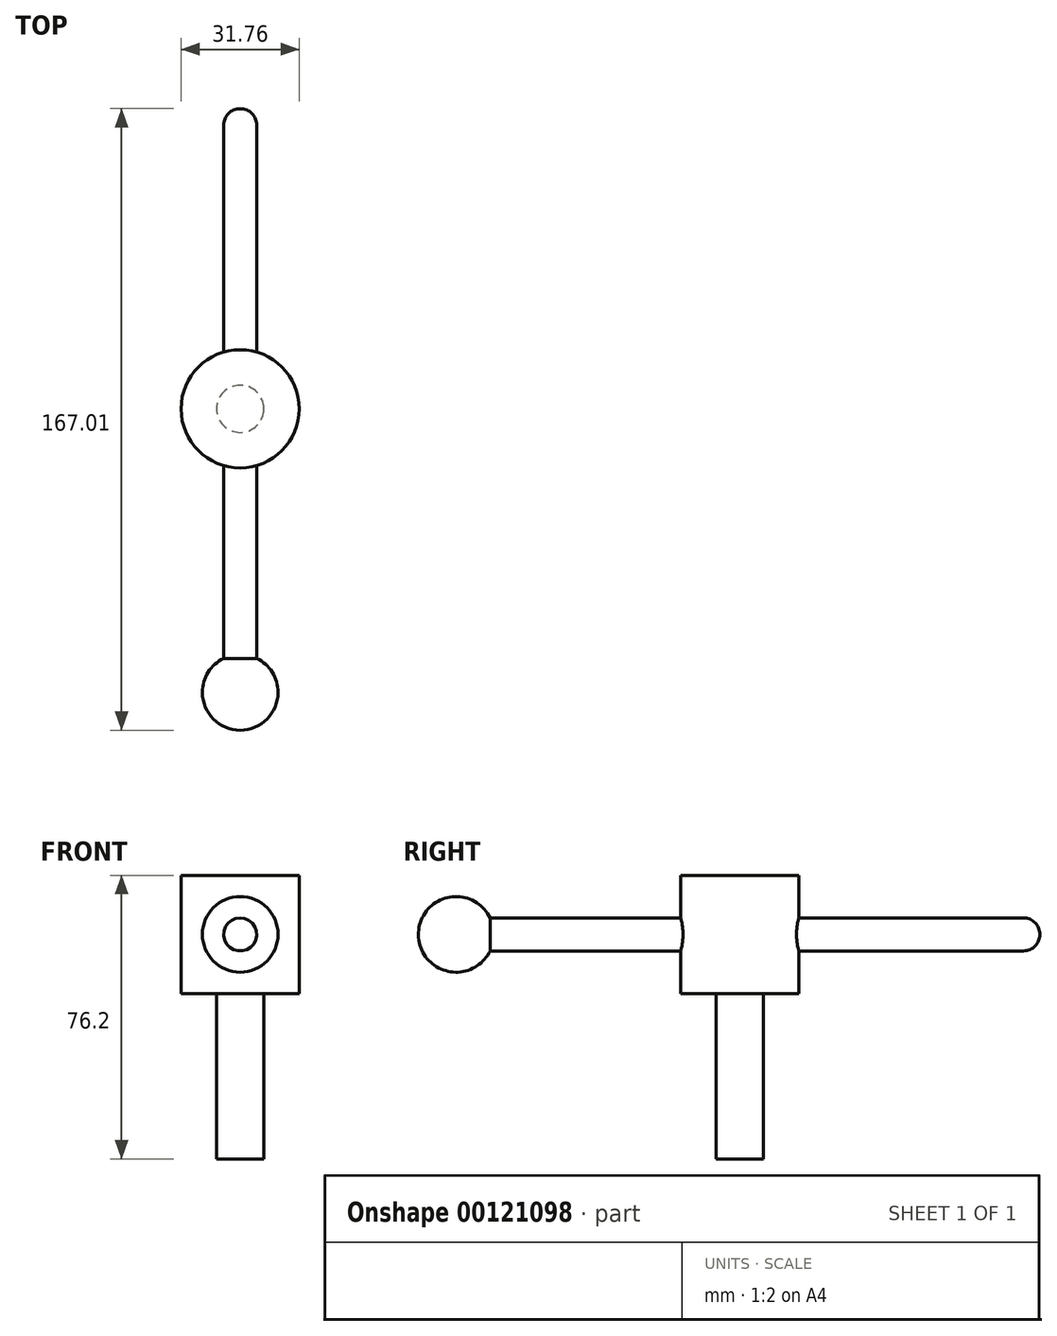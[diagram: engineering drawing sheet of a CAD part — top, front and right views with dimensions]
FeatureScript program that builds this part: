
annotation { "Feature Type Name" : "Feature", "Feature Type Description" : "" }
export const myFeature = defineFeature(function(context is Context, id is Id, definition is map)
    precondition{}
    {
        {
            var Q0;
            Q0=qCreatedBy(makeId("Right.planeOp"),FACE);
            var sketch = newSketch(context, id + "F0", { "sketchPlane" : qUnion([Q0])});
            skLineSegment(sketch, "E0.bottom", {"start": v(0, 0) * mm, "end": v(-6.35, 0) * mm});
            skLineSegment(sketch, "E0.top", {"start": v(0, 76.2) * mm, "end": v(-15.88, 76.2) * mm});
            skLineSegment(sketch, "E0.left", {"start": v(0, 0) * mm, "end": v(0, 76.2) * mm});
            skLineSegment(sketch, "E0.right", {"start": v(-15.88, 44.45) * mm, "end": v(-15.88, 76.2) * mm});
            skLineSegment(sketch, "E1", {"start": v(-15.88, 44.45) * mm, "end": v(-6.35, 44.45) * mm});
            skLineSegment(sketch, "E2", {"start": v(-6.35, 44.45) * mm, "end": v(-6.35, 0) * mm});
            skSolve(sketch);
        }
        {
            var Q0;
            Q0 = qSketchRegion(id + "F0", true);
            var Q1;
            Q1=sQuery(id+"F0.wireOp",EDGE,"E0.left");
            revolve(context, id + "F1", {"entities" : qUnion([Q0]), "axis" : qUnion([Q1]), "revolveType" : RevolveType.FULL});
        }
        {
            var Q0;
            Q0=qCreatedBy(makeId("Front.planeOp"),FACE);
            var sketch = newSketch(context, id + "F2", { "sketchPlane" : qUnion([Q0])});
            skCircle(sketch, "E3", {"center": v(0, 60.33) * mm, "radius": 4.45 * mm});
            skSolve(sketch);
        }
        {
            var Q0;
            Q0 = qSketchRegion(id + "F2", true);
            extrude(context, id + "F3", {"entities" : qUnion([Q0]), "operationType" : NewBodyOperationType.ADD, "endBound" : BoundingType.SYMMETRIC, "depth" : 152.4 * mm});
        }
        {
            var Q0;
            Q0=makeQuery(id+"F3.opExtrude","CAP_FACE",FACE,{"disambiguationData":[OSD([sQuery(id+"F2.wireOp",EDGE,"E3")])],"isStart":true});
            var sketch = newSketch(context, id + "F4", { "sketchPlane" : qUnion([Q0])});
            skArc(sketch, "E4", {"start": v(-10.16, 60.33) * mm, "mid": v(0, 70.48) * mm, "end": v(10.16, 60.33) * mm});
            skLineSegment(sketch, "E5", {"start": v(-10.16, 60.33) * mm, "end": v(10.16, 60.33) * mm});
            skSolve(sketch);
        }
        {
            var Q0;
            {var subQ0=sQuery(id+"F4.wireOp",EDGE,"E4");Q0=makeQuery(id+"F4.imprint","IMPRINT",FACE,{"disambiguationData":[TD([[makeQuery(id+"F4.imprint","IMPRINT",EDGE,{"derivedFrom":subQ0}),-1.0]])]});}
            var Q1;
            {var subQ0=sQuery(id+"F4.wireOp",EDGE,"E5");var subQ1=makeQuery(id+"F3.opExtrude","CAP_EDGE",EDGE,{"disambiguationData":[OSD([sQuery(id+"F2.wireOp",EDGE,"E3")])],"isStart":true});var subQ2=makeQuery(id+"F4.imprint","INTERSECT",VERTEX,{"disambiguationData":[OD(0.0)],"derivedFrom":[subQ1,subQ0]});Q1=makeQuery(id+"F4.imprint","IMPRINT",FACE,{"disambiguationData":[TD([[makeQuery(id+"F4.imprint","IMPRINT",EDGE,{"disambiguationData":[TD([[subQ2,-1.0]])],"derivedFrom":subQ0}),1.0]])]});}
            var Q2;
            Q2=sQuery(id+"F4.wireOp",EDGE,"E5");
            revolve(context, id + "F5", {"operationType" : NewBodyOperationType.ADD, "entities" : qUnion([Q0, Q1]), "axis" : qUnion([Q2]), "revolveType" : RevolveType.FULL});
        }
        {
            var Q0;
            Q0=makeQuery(id+"F3.opExtrude","CAP_FACE",FACE,{"disambiguationData":[OSD([sQuery(id+"F2.wireOp",EDGE,"E3")])],"isStart":false});
            var sketch = newSketch(context, id + "F6", { "sketchPlane" : qUnion([Q0])});
            skArc(sketch, "E6", {"start": v(-10.16, 60.33) * mm, "mid": v(0, 70.48) * mm, "end": v(10.16, 60.33) * mm});
            skLineSegment(sketch, "E7", {"start": v(-10.16, 60.33) * mm, "end": v(10.16, 60.33) * mm});
            skSolve(sketch);
        }
        {
            var Q0;
            Q0 = qSketchRegion(id + "F6", true);
            var Q1;
            Q1=sQuery(id+"F6.wireOp",EDGE,"E7");
            revolve(context, id + "F7", {"operationType" : NewBodyOperationType.ADD, "entities" : qUnion([Q0]), "axis" : qUnion([Q1]), "revolveType" : RevolveType.FULL});
        }
    });
